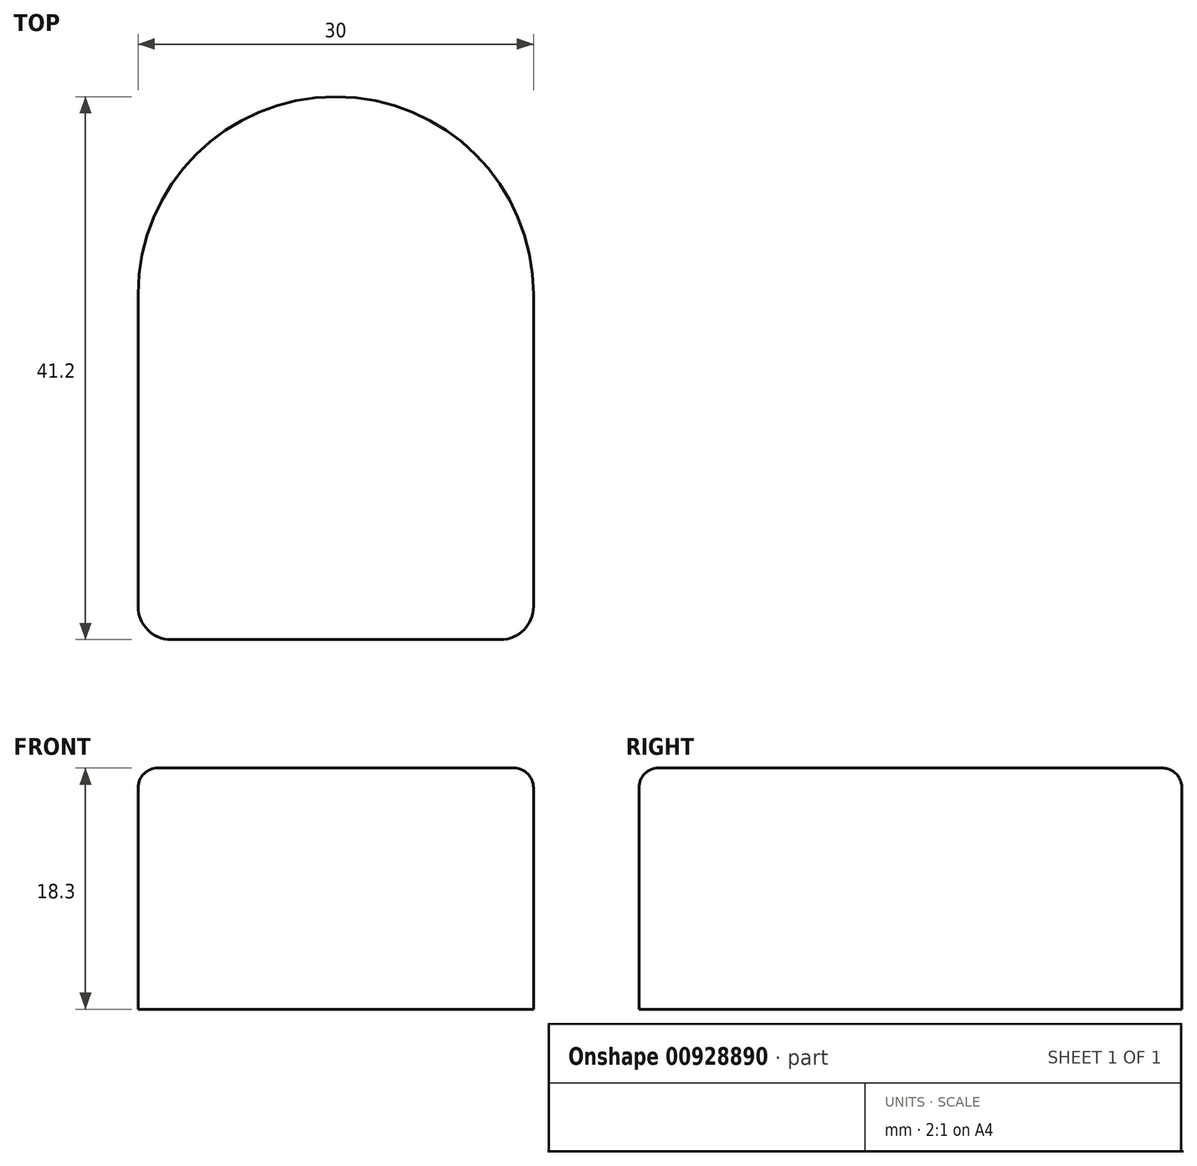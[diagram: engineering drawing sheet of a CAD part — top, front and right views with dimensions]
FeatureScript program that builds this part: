
annotation { "Feature Type Name" : "Feature", "Feature Type Description" : "" }
export const myFeature = defineFeature(function(context is Context, id is Id, definition is map)
    precondition{}
    {
        {
            var Q0;
            Q0=qCreatedBy(makeId("Top.planeOp"),FACE);
            var sketch = newSketch(context, id + "F0", { "sketchPlane" : qUnion([Q0])});
            skLineSegment(sketch, "E0.top", {"start": v(-9.4, 0) * mm, "end": v(15.6, 0) * mm});
            skLineSegment(sketch, "E0.left", {"start": v(-11.9, 26.2) * mm, "end": v(-11.9, 2.5) * mm});
            skLineSegment(sketch, "E0.right", {"start": v(18.1, 26.2) * mm, "end": v(18.1, 2.5) * mm});
            skArc(sketch, "E1", {"start": v(18.1, 26.2) * mm, "mid": v(3.1, 41.2) * mm, "end": v(-11.9, 26.2) * mm});
            skPoint(sketch, "E2.visualSharp", {"position": v(-11.9, 0) * mm});
            skArc(sketch, "E2.filletArc", {"start": v(-11.9, 2.5) * mm, "mid": v(-11.17, 0.73) * mm, "end": v(-9.4, 0) * mm});
            skPoint(sketch, "E3.visualSharp", {"position": v(18.1, 0) * mm});
            skArc(sketch, "E3.filletArc", {"start": v(15.6, 0) * mm, "mid": v(17.37, 0.73) * mm, "end": v(18.1, 2.5) * mm});
            skSolve(sketch);
        }
        {
            var Q0;
            Q0=qSketchRegion(id+"F0",true);
            extrude(context, id + "F1", {"entities" : qUnion([Q0]), "depth" : 18.3 * mm, "offsetDistance" : 25 * mm});
        }
        {
            var Q0;
            Q0=makeQuery(id+"F1.opExtrude","CAP_FACE",FACE,{"disambiguationData":[OSD([sQuery(id+"F0.wireOp",EDGE,"E0.top"),sQuery(id+"F0.wireOp",EDGE,"E0.left"),sQuery(id+"F0.wireOp",EDGE,"E0.right"),sQuery(id+"F0.wireOp",EDGE,"E1"),sQuery(id+"F0.wireOp",EDGE,"E2.filletArc"),sQuery(id+"F0.wireOp",EDGE,"E3.filletArc")])],"isStart":false});
            fillet(context, id + "F2", {"entities" : qUnion([Q0]), "radius" : 1.5 * mm, "tangentPropagation" : true, "allowEdgeOverflow" : false});
        }
    });
